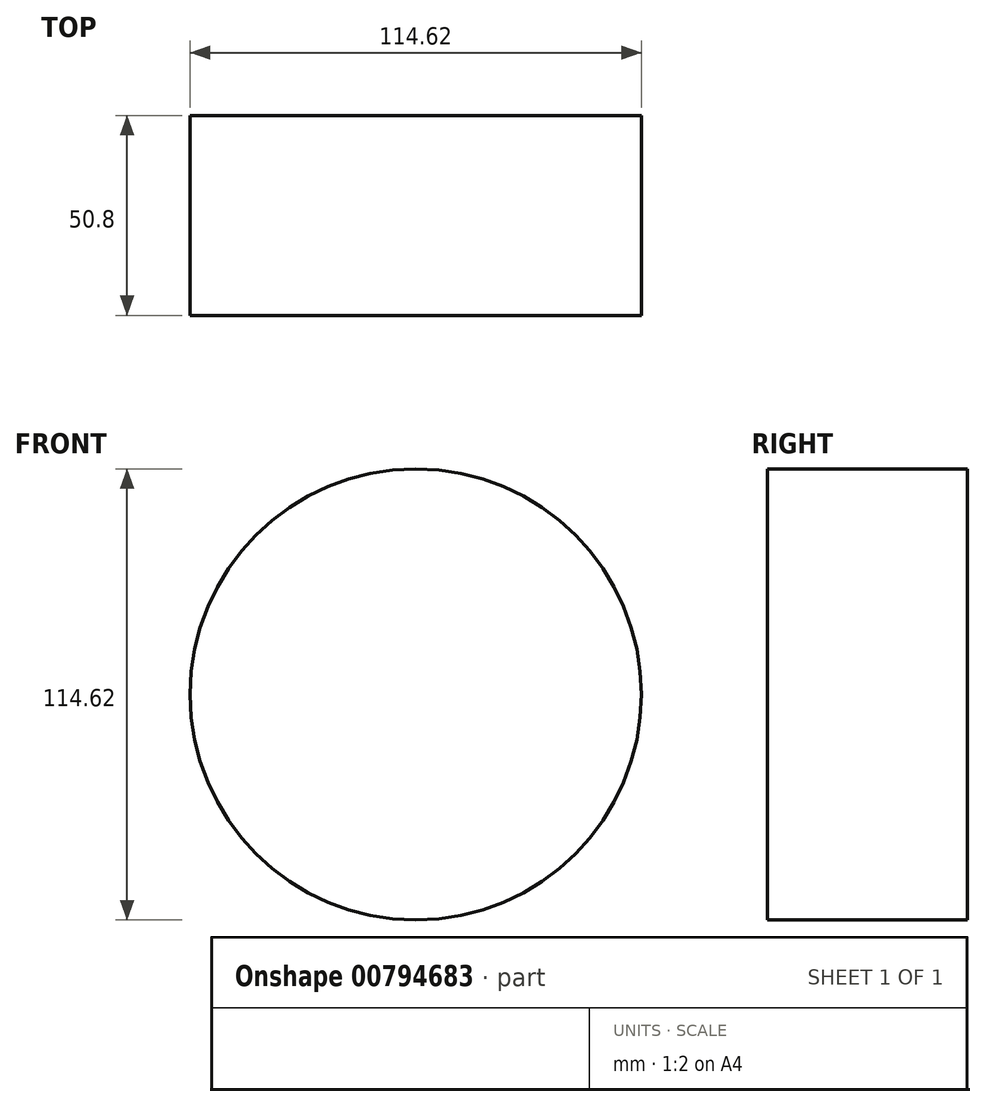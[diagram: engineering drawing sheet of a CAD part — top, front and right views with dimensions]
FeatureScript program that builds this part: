
annotation { "Feature Type Name" : "Feature", "Feature Type Description" : "" }
export const myFeature = defineFeature(function(context is Context, id is Id, definition is map)
    precondition{}
    {
        {
            var Q0;
            Q0=qCreatedBy(makeId("Front.planeOp"),FACE);
            var sketch = newSketch(context, id + "F0", { "sketchPlane" : qUnion([Q0])});
            skCircle(sketch, "E0", {"center": v(0, 0) * mm, "radius": 28.66 * mm});
            skSolve(sketch);
        }
        {
            var Q0;
            Q0=makeQuery(id+"F0.imprint","IMPRINT",FACE,{"disambiguationData":[TD([[makeQuery(id+"F0.imprint","IMPRINT",EDGE,{"derivedFrom":sQuery(id+"F0.wireOp",EDGE,"E0")}),1.0]])]});
            extrude(context, id + "F1", {"entities" : qUnion([Q0]), "depth" : 25.4 * mm, "offsetDistance" : 25.4 * mm});
        }
        {
            var Q0;
            Q0=makeQuery(id+"F1.opExtrude","SWEPT_BODY",BODY,{"disambiguationData":[OSD([sQuery(id+"F0.wireOp",EDGE,"E0")])]});
            var Q1;
            Q1=qCreatedBy(makeId("Origin.pointOp"),VERTEX);
            transform(context, id + "F2", {"entities" : qUnion([Q0]), "transformType" : TransformType.SCALE_UNIFORMLY, "scale" : 2, "scalePoint" : qUnion([Q1]), "makeCopy" : false});
        }
    });
